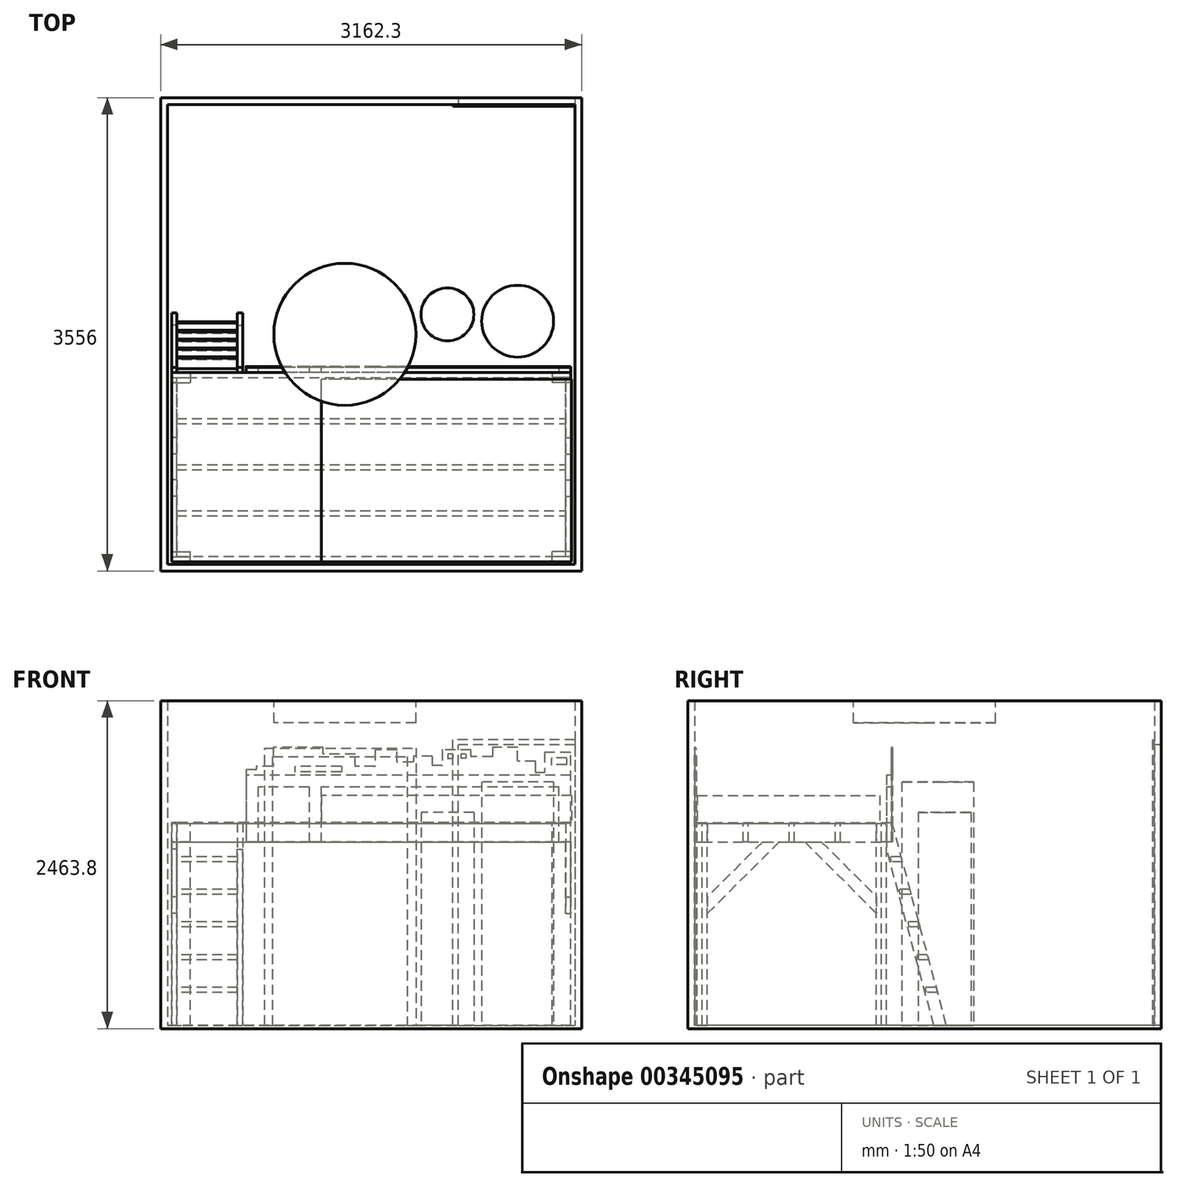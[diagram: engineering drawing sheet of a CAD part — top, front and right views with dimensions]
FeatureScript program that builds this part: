
annotation { "Feature Type Name" : "Feature", "Feature Type Description" : "" }
export const myFeature = defineFeature(function(context is Context, id is Id, definition is map)
    precondition{}
    {
        {
            var Q0;
            Q0=qCreatedBy(makeId("Top.planeOp"),FACE);
            var sketch = newSketch(context, id + "F0", { "sketchPlane" : qUnion([Q0])});
            skLineSegment(sketch, "E0.bottom", {"start": v(-2262.88, 2923.08) * mm, "end": v(-56.88, 2923.08) * mm});
            skLineSegment(sketch, "E0.top", {"start": v(-2262.88, -531.32) * mm, "end": v(797.82, -531.32) * mm});
            skLineSegment(sketch, "E0.left", {"start": v(-2262.88, 2923.08) * mm, "end": v(-2262.88, -531.32) * mm});
            skLineSegment(sketch, "E0.right", {"start": v(797.82, 2923.08) * mm, "end": v(797.82, -531.32) * mm});
            skLineSegment(sketch, "E1.0", {"start": v(-2313.68, 2973.88) * mm, "end": v(-56.88, 2973.88) * mm});
            skLineSegment(sketch, "E1.1", {"start": v(-2313.68, 2973.88) * mm, "end": v(-2313.68, -582.12) * mm});
            skLineSegment(sketch, "E1.2", {"start": v(-2313.68, -582.12) * mm, "end": v(848.62, -582.12) * mm});
            skLineSegment(sketch, "E1.3", {"start": v(848.62, 2973.88) * mm, "end": v(848.62, -582.12) * mm});
            skLineSegment(sketch, "E2.bottom", {"start": v(-94.98, 2923.08) * mm, "end": v(-56.88, 2923.08) * mm});
            skLineSegment(sketch, "E2.top", {"start": v(-94.98, 2910.38) * mm, "end": v(-56.88, 2910.38) * mm});
            skLineSegment(sketch, "E2.left", {"start": v(-94.98, 2923.08) * mm, "end": v(-94.98, 2910.38) * mm});
            skLineSegment(sketch, "E2.right", {"start": v(-56.88, 2923.08) * mm, "end": v(-56.88, 2910.38) * mm});
            skLineSegment(sketch, "E3", {"start": v(-56.88, 2923.08) * mm, "end": v(-56.88, 2973.88) * mm});
            skLineSegment(sketch, "E4", {"start": v(848.62, 2973.88) * mm, "end": v(797.82, 2973.88) * mm});
            skLineSegment(sketch, "E5", {"start": v(797.82, 2973.88) * mm, "end": v(797.82, 2923.08) * mm});
            skLineSegment(sketch, "E6", {"start": v(-56.88, 2973.88) * mm, "end": v(797.82, 2973.88) * mm});
            skLineSegment(sketch, "E7", {"start": v(797.82, 2923.08) * mm, "end": v(-56.88, 2923.08) * mm});
            skSolve(sketch);
        }
        {
            var Q0;
            Q0 = qSketchRegion(id + "F0", true);
            extrude(context, id + "F1", {"entities" : qUnion([Q0]), "depth" : 2438.4 * mm});
        }
        {
            var Q0;
            Q0=makeQuery(id+"F1.opExtrude","SWEPT_FACE",FACE,{"disambiguationData":[OSD([sQuery(id+"F0.wireOp",EDGE,"E0.bottom"),sQuery(id+"F0.wireOp",EDGE,"E2.bottom"),sQuery(id+"F0.wireOp",EDGE,"E7")])]});
            var sketch = newSketch(context, id + "F2", { "sketchPlane" : qUnion([Q0])});
            skLineSegment(sketch, "E8.bottom", {"start": v(797.82, 0) * mm, "end": v(-78.48, 0) * mm});
            skLineSegment(sketch, "E8.top", {"start": v(797.82, 2108.2) * mm, "end": v(-78.48, 2108.2) * mm});
            skLineSegment(sketch, "E8.left", {"start": v(797.82, 0) * mm, "end": v(797.82, 2108.2) * mm});
            skLineSegment(sketch, "E8.right", {"start": v(-78.48, 0) * mm, "end": v(-78.48, 2108.2) * mm});
            skSolve(sketch);
        }
        {
            var Q0;
            Q0 = qSketchRegion(id + "F2", true);
            extrude(context, id + "F3", {"entities" : qUnion([Q0]), "operationType" : NewBodyOperationType.REMOVE, "endBound" : BoundingType.UP_TO_NEXT, "oppositeDirection" : true, "depth" : 25.4 * mm});
        }
        {
            var Q0;
            Q0=makeQuery(id+"F1.opExtrude","SWEPT_FACE",FACE,{"disambiguationData":[OSD([sQuery(id+"F0.wireOp",EDGE,"E0.bottom"),sQuery(id+"F0.wireOp",EDGE,"E2.bottom"),sQuery(id+"F0.wireOp",EDGE,"E7")])]});
            var sketch = newSketch(context, id + "F4", { "sketchPlane" : qUnion([Q0])});
            skLineSegment(sketch, "E9.bottom", {"start": v(-78.48, 0) * mm, "end": v(-116.58, 0) * mm});
            skLineSegment(sketch, "E9.top", {"start": v(-78.48, 2146.3) * mm, "end": v(-116.58, 2146.3) * mm});
            skLineSegment(sketch, "E9.left", {"start": v(-78.48, 0) * mm, "end": v(-78.48, 2146.3) * mm});
            skLineSegment(sketch, "E9.right", {"start": v(-116.58, 0) * mm, "end": v(-116.58, 2146.3) * mm});
            skLineSegment(sketch, "E10.bottom", {"start": v(-78.48, 2146.3) * mm, "end": v(797.82, 2146.3) * mm});
            skLineSegment(sketch, "E10.top", {"start": v(-78.48, 2108.2) * mm, "end": v(797.82, 2108.2) * mm});
            skLineSegment(sketch, "E10.left", {"start": v(-78.48, 2146.3) * mm, "end": v(-78.48, 2108.2) * mm});
            skLineSegment(sketch, "E10.right", {"start": v(797.82, 2146.3) * mm, "end": v(797.82, 2108.2) * mm});
            skSolve(sketch);
        }
        {
            var Q0;
            Q0 = qSketchRegion(id + "F4", true);
            extrude(context, id + "F5", {"entities" : qUnion([Q0]), "operationType" : NewBodyOperationType.ADD, "depth" : 12.7 * mm});
        }
        {
            var Q0;
            Q0=makeQuery(id+"F1.opExtrude","CAP_FACE",FACE,{"disambiguationData":[OSD([sQuery(id+"F0.wireOp",EDGE,"E0.bottom"),sQuery(id+"F0.wireOp",EDGE,"E0.top"),sQuery(id+"F0.wireOp",EDGE,"E0.left"),sQuery(id+"F0.wireOp",EDGE,"E0.right"),sQuery(id+"F0.wireOp",EDGE,"E1.0"),sQuery(id+"F0.wireOp",EDGE,"E1.1"),sQuery(id+"F0.wireOp",EDGE,"E1.2"),sQuery(id+"F0.wireOp",EDGE,"E1.3"),sQuery(id+"F0.wireOp",EDGE,"E2.bottom"),sQuery(id+"F0.wireOp",EDGE,"E4"),sQuery(id+"F0.wireOp",EDGE,"E6"),sQuery(id+"F0.wireOp",EDGE,"E7")])],"isStart":false});
            var sketch = newSketch(context, id + "F6", { "sketchPlane" : qUnion([Q0])});
            skCircle(sketch, "E11", {"center": v(-929.38, 1195.88) * mm, "radius": 533.4 * mm});
            skSolve(sketch);
        }
        {
            var Q0;
            Q0 = qSketchRegion(id + "F6", true);
            extrude(context, id + "F7", {"entities" : qUnion([Q0]), "oppositeDirection" : true, "depth" : 165.1 * mm});
        }
        {
            var Q0;
            Q0=makeQuery(id+"F5.boolean.opBoolean","MERGE",FACE,{"derivedFrom":[makeQuery(id+"F1.opExtrude","CAP_FACE",FACE,{"disambiguationData":[OSD([sQuery(id+"F0.wireOp",EDGE,"E0.bottom"),sQuery(id+"F0.wireOp",EDGE,"E0.top"),sQuery(id+"F0.wireOp",EDGE,"E0.left"),sQuery(id+"F0.wireOp",EDGE,"E0.right"),sQuery(id+"F0.wireOp",EDGE,"E1.0"),sQuery(id+"F0.wireOp",EDGE,"E1.1"),sQuery(id+"F0.wireOp",EDGE,"E1.2"),sQuery(id+"F0.wireOp",EDGE,"E1.3"),sQuery(id+"F0.wireOp",EDGE,"E2.bottom"),sQuery(id+"F0.wireOp",EDGE,"E4"),sQuery(id+"F0.wireOp",EDGE,"E6"),sQuery(id+"F0.wireOp",EDGE,"E7")])],"isStart":true}),makeQuery(id+"F5.opExtrude","SWEPT_FACE",FACE,{"disambiguationData":[OSD([sQuery(id+"F4.wireOp",EDGE,"E9.bottom")])]})]});
            var sketch = newSketch(context, id + "F8", { "sketchPlane" : qUnion([Q0])});
            skLineSegment(sketch, "E12.bottom", {"start": v(-2313.68, -2973.88) * mm, "end": v(848.62, -2973.88) * mm});
            skLineSegment(sketch, "E12.top", {"start": v(-2313.68, 582.12) * mm, "end": v(848.62, 582.12) * mm});
            skLineSegment(sketch, "E12.left", {"start": v(-2313.68, -2973.88) * mm, "end": v(-2313.68, 582.12) * mm});
            skLineSegment(sketch, "E12.right", {"start": v(848.62, -2973.88) * mm, "end": v(848.62, 582.12) * mm});
            skSolve(sketch);
        }
        {
            var Q0;
            Q0 = qSketchRegion(id + "F8", true);
            extrude(context, id + "F9", {"entities" : qUnion([Q0]), "operationType" : NewBodyOperationType.ADD, "depth" : 25.4 * mm});
        }
        {
            var Q0;
            Q0=makeQuery(id+"F9.opExtrude","CAP_FACE",FACE,{"disambiguationData":[OSD([sQuery(id+"F8.wireOp",EDGE,"E12.bottom"),sQuery(id+"F8.wireOp",EDGE,"E12.top"),sQuery(id+"F8.wireOp",EDGE,"E12.left"),sQuery(id+"F8.wireOp",EDGE,"E12.right")])],"isStart":true});
            cPlane(context, id + "F10", {"entities" : qUnion([Q0]), "cplaneType" : CPlaneType.OFFSET, "offset" : 1524 * mm, "width" : 152.4 * mm, "height" : 152.4 * mm});
        }
        {
            var Q0;
            Q0=makeQuery(id+"F1.opExtrude","SWEPT_FACE",FACE,{"disambiguationData":[OSD([sQuery(id+"F0.wireOp",EDGE,"E0.top")])]});
            var sketch = newSketch(context, id + "F11", { "sketchPlane" : qUnion([Q0])});
            skLineSegment(sketch, "E13.bottom", {"start": v(1532.63, 0) * mm, "end": v(1469.13, 0) * mm});
            skLineSegment(sketch, "E13.top", {"start": v(1532.63, 2082.8) * mm, "end": v(1469.13, 2082.8) * mm});
            skLineSegment(sketch, "E13.left", {"start": v(1532.63, 0) * mm, "end": v(1532.63, 2082.8) * mm});
            skLineSegment(sketch, "E13.right", {"start": v(1469.13, 0) * mm, "end": v(1469.13, 2082.8) * mm});
            skLineSegment(sketch, "E14.bottom", {"start": v(1469.13, 2082.8) * mm, "end": v(459.48, 2082.8) * mm});
            skLineSegment(sketch, "E14.top", {"start": v(1469.13, 2019.3) * mm, "end": v(459.48, 2019.3) * mm});
            skLineSegment(sketch, "E14.left", {"start": v(1469.13, 2082.8) * mm, "end": v(1469.13, 2019.3) * mm});
            skLineSegment(sketch, "E14.right", {"start": v(459.48, 2082.8) * mm, "end": v(459.48, 2019.3) * mm});
            skLineSegment(sketch, "E15.bottom", {"start": v(459.48, 2082.8) * mm, "end": v(395.98, 2082.8) * mm});
            skLineSegment(sketch, "E15.top", {"start": v(459.48, 0) * mm, "end": v(395.98, 0) * mm});
            skLineSegment(sketch, "E15.left", {"start": v(459.48, 2082.8) * mm, "end": v(459.48, 0) * mm});
            skLineSegment(sketch, "E15.right", {"start": v(395.98, 2082.8) * mm, "end": v(395.98, 0) * mm});
            skSolve(sketch);
        }
        {
            var Q0;
            Q0 = qSketchRegion(id + "F11", true);
            extrude(context, id + "F12", {"entities" : qUnion([Q0]), "operationType" : NewBodyOperationType.ADD, "depth" : 12.7 * mm});
        }
        {
            var Q0;
            Q0=qCreatedBy(id+"F10.planeOp",FACE);
            var sketch = newSketch(context, id + "F13", { "sketchPlane" : qUnion([Q0])});
            skLineSegment(sketch, "E16.bottom", {"start": v(772.42, -512.27) * mm, "end": v(-1107.18, -512.27) * mm});
            skLineSegment(sketch, "E16.top", {"start": v(772.42, 859.33) * mm, "end": v(-1107.18, 859.33) * mm});
            skLineSegment(sketch, "E16.left", {"start": v(772.42, -512.27) * mm, "end": v(772.42, 859.33) * mm});
            skLineSegment(sketch, "E16.right", {"start": v(-1107.18, -512.27) * mm, "end": v(-1107.18, 859.33) * mm});
            skSolve(sketch);
        }
        {
            var Q0;
            Q0 = qSketchRegion(id + "F13", true);
            extrude(context, id + "F14", {"entities" : qUnion([Q0]), "depth" : 203.2 * mm});
        }
        {
            var Q0;
            Q0=qCreatedBy(id+"F10.planeOp",FACE);
            var sketch = newSketch(context, id + "F15", { "sketchPlane" : qUnion([Q0])});
            skLineSegment(sketch, "E17.bottom", {"start": v(766.07, -512.27) * mm, "end": v(-2231.13, -512.27) * mm});
            skLineSegment(sketch, "E17.top", {"start": v(766.07, 910.13) * mm, "end": v(-2231.13, 910.13) * mm});
            skLineSegment(sketch, "E17.left", {"start": v(766.07, -512.27) * mm, "end": v(766.07, 910.13) * mm});
            skLineSegment(sketch, "E17.right", {"start": v(-2231.13, -512.27) * mm, "end": v(-2231.13, 910.13) * mm});
            skSolve(sketch);
        }
        {
            var Q0;
            Q0 = qSketchRegion(id + "F15", true);
            extrude(context, id + "F16", {"entities" : qUnion([Q0]), "oppositeDirection" : true, "depth" : 6.35 * mm});
        }
        {
            var Q0;
            Q0=makeQuery(id+"F16.opExtrude","CAP_FACE",FACE,{"disambiguationData":[OSD([sQuery(id+"F15.wireOp",EDGE,"E17.bottom"),sQuery(id+"F15.wireOp",EDGE,"E17.top"),sQuery(id+"F15.wireOp",EDGE,"E17.left"),sQuery(id+"F15.wireOp",EDGE,"E17.right")])],"isStart":false});
            var sketch = newSketch(context, id + "F17", { "sketchPlane" : qUnion([Q0])});
            skLineSegment(sketch, "E18.bottom", {"start": v(-2231.13, 474.17) * mm, "end": v(-2193.03, 474.17) * mm});
            skLineSegment(sketch, "E18.top", {"start": v(-2231.13, -872.03) * mm, "end": v(-2193.03, -872.03) * mm});
            skLineSegment(sketch, "E18.left", {"start": v(-2231.13, 474.17) * mm, "end": v(-2231.13, -872.03) * mm});
            skLineSegment(sketch, "E18.right", {"start": v(-2193.03, 474.17) * mm, "end": v(-2193.03, -872.03) * mm});
            skLineSegment(sketch, "E19.bottom", {"start": v(766.07, 474.17) * mm, "end": v(727.97, 474.17) * mm});
            skLineSegment(sketch, "E19.top", {"start": v(766.07, -872.03) * mm, "end": v(727.97, -872.03) * mm});
            skLineSegment(sketch, "E19.left", {"start": v(766.07, 474.17) * mm, "end": v(766.07, -872.03) * mm});
            skLineSegment(sketch, "E19.right", {"start": v(727.97, 474.17) * mm, "end": v(727.97, -872.03) * mm});
            skLineSegment(sketch, "E20.0", {"start": v(-2231.13, 512.27) * mm, "end": v(-2231.13, -910.13) * mm, "construction": true});
            skLineSegment(sketch, "E21.0", {"start": v(766.07, 512.27) * mm, "end": v(766.07, -910.13) * mm, "construction": true});
            skSolve(sketch);
        }
        {
            var Q0;
            Q0 = qSketchRegion(id + "F17", true);
            extrude(context, id + "F18", {"entities" : qUnion([Q0]), "depth" : 139.7 * mm});
        }
        {
            var Q0;
            Q0=makeQuery(id+"F16.opExtrude","CAP_FACE",FACE,{"disambiguationData":[OSD([sQuery(id+"F15.wireOp",EDGE,"E17.bottom"),sQuery(id+"F15.wireOp",EDGE,"E17.top"),sQuery(id+"F15.wireOp",EDGE,"E17.left"),sQuery(id+"F15.wireOp",EDGE,"E17.right")])],"isStart":false});
            var sketch = newSketch(context, id + "F19", { "sketchPlane" : qUnion([Q0])});
            skPoint(sketch, "E22.0", {"position": v(-2193.03, 474.17) * mm});
            skPoint(sketch, "E23.0", {"position": v(727.97, 474.17) * mm});
            skPoint(sketch, "E24.0", {"position": v(766.07, -910.13) * mm});
            skPoint(sketch, "E25.0", {"position": v(-2231.13, -910.13) * mm});
            skLineSegment(sketch, "E26.0", {"start": v(766.07, 512.27) * mm, "end": v(-2231.13, 512.27) * mm, "construction": true});
            skLineSegment(sketch, "E27.top", {"start": v(-2231.13, -872.03) * mm, "end": v(766.07, -872.03) * mm});
            skLineSegment(sketch, "E27.right", {"start": v(766.07, -910.13) * mm, "end": v(766.07, -872.03) * mm});
            skLineSegment(sketch, "E28", {"start": v(766.07, -910.13) * mm, "end": v(-2231.13, -910.13) * mm});
            skLineSegment(sketch, "E29", {"start": v(-2231.13, -910.13) * mm, "end": v(-2231.13, -872.03) * mm});
            skLineSegment(sketch, "E30", {"start": v(766.07, -872.03) * mm, "end": v(766.07, -910.13) * mm});
            skLineSegment(sketch, "E31.0.1.0", {"start": v(-2231.13, 512.27) * mm, "end": v(766.07, 512.27) * mm});
            skLineSegment(sketch, "E31.0.1.1", {"start": v(766.07, 474.17) * mm, "end": v(-2231.13, 474.17) * mm});
            skLineSegment(sketch, "E31.0.1.2", {"start": v(766.07, 512.27) * mm, "end": v(766.07, 474.17) * mm});
            skLineSegment(sketch, "E31.0.1.3", {"start": v(-2231.13, 474.17) * mm, "end": v(-2231.13, 512.27) * mm});
            skLineSegment(sketch, "E31.direction1", {"start": v(-2231.13, -872.03) * mm, "end": v(-2165.04, -872.03) * mm, "construction": true});
            skLineSegment(sketch, "E31.direction2", {"start": v(-2231.13, -872.03) * mm, "end": v(-2231.13, 512.27) * mm, "construction": true});
            skPoint(sketch, "E32.0", {"position": v(-2231.13, -872.03) * mm});
            skPoint(sketch, "E33.0", {"position": v(766.07, -872.03) * mm});
            skPoint(sketch, "E34.startSnap0", {"position": v(-732.53, 512.27) * mm});
            skLineSegment(sketch, "E35.0", {"start": v(-2193.03, 474.17) * mm, "end": v(-2193.03, -872.03) * mm, "construction": true});
            skLineSegment(sketch, "E36.0", {"start": v(727.97, 474.17) * mm, "end": v(727.97, -872.03) * mm, "construction": true});
            skLineSegment(sketch, "E37.bottom", {"start": v(-2193.03, -179.88) * mm, "end": v(727.97, -179.88) * mm});
            skLineSegment(sketch, "E37.top", {"start": v(-2193.03, -217.98) * mm, "end": v(727.97, -217.98) * mm});
            skLineSegment(sketch, "E37.left", {"start": v(-2193.03, -179.88) * mm, "end": v(-2193.03, -217.98) * mm});
            skLineSegment(sketch, "E37.right", {"start": v(727.97, -179.88) * mm, "end": v(727.97, -217.98) * mm});
            skPoint(sketch, "E38", {"position": v(-2193.03, -198.93) * mm});
            skPoint(sketch, "E39", {"position": v(727.97, -198.93) * mm});
            skLineSegment(sketch, "E40", {"start": v(-732.53, -179.88) * mm, "end": v(-732.53, 474.17) * mm, "construction": true});
            skLineSegment(sketch, "E41", {"start": v(-732.53, -872.03) * mm, "end": v(-732.53, -217.98) * mm, "construction": true});
            skPoint(sketch, "E42", {"position": v(-732.53, 147.15) * mm});
            skLineSegment(sketch, "E43.left", {"start": v(727.97, 0) * mm, "end": v(727.97, 294.3) * mm});
            skLineSegment(sketch, "E43.right", {"start": v(-2193.03, 0) * mm, "end": v(-2193.03, 294.3) * mm});
            skLineSegment(sketch, "E44.bottom", {"start": v(-2193.03, 128.1) * mm, "end": v(727.97, 128.1) * mm});
            skLineSegment(sketch, "E44.top", {"start": v(-2193.03, 166.2) * mm, "end": v(727.97, 166.2) * mm});
            skLineSegment(sketch, "E44.left", {"start": v(-2193.03, 128.1) * mm, "end": v(-2193.03, 166.2) * mm});
            skLineSegment(sketch, "E44.right", {"start": v(727.97, 128.1) * mm, "end": v(727.97, 166.2) * mm});
            skLineSegment(sketch, "E45", {"start": v(-2193.03, -198.93) * mm, "end": v(727.97, -198.93) * mm, "construction": true});
            skLineSegment(sketch, "E46.MirrorCS", {"start": v(-2193.03, -525.95) * mm, "end": v(727.97, -525.95) * mm});
            skLineSegment(sketch, "E47.MirrorCS", {"start": v(-2193.03, -564.05) * mm, "end": v(727.97, -564.05) * mm});
            skLineSegment(sketch, "E48", {"start": v(-2193.03, -525.95) * mm, "end": v(-2193.03, -564.05) * mm, "construction": true});
            skLineSegment(sketch, "E49", {"start": v(-2193.03, -525.95) * mm, "end": v(-2193.03, -564.05) * mm});
            skLineSegment(sketch, "E50", {"start": v(727.97, -525.95) * mm, "end": v(727.97, -564.05) * mm});
            skSolve(sketch);
        }
        {
            var Q0;
            Q0 = qSketchRegion(id + "F19", true);
            extrude(context, id + "F20", {"entities" : qUnion([Q0]), "depth" : 139.7 * mm});
        }
        {
            var Q0;
            Q0=makeQuery(id+"F18.opExtrude","SWEPT_FACE",FACE,{"disambiguationData":[OSD([sQuery(id+"F17.wireOp",EDGE,"E18.left")])]});
            var sketch = newSketch(context, id + "F21", { "sketchPlane" : qUnion([Q0])});
            skPoint(sketch, "E51.0", {"position": v(-910.13, 1524) * mm});
            skPoint(sketch, "E52.0", {"position": v(-910.13, 1377.95) * mm});
            skLineSegment(sketch, "E53", {"start": v(-910.13, 1524) * mm, "end": v(-948.23, 1524) * mm});
            skLineSegment(sketch, "E54", {"start": v(-948.23, 1524) * mm, "end": v(-1356.58, 0) * mm});
            skLineSegment(sketch, "E55", {"start": v(-1356.58, 0) * mm, "end": v(-1264.54, 0) * mm});
            skLineSegment(sketch, "E56", {"start": v(-1264.54, 0) * mm, "end": v(-910.13, 1322.7) * mm});
            skLineSegment(sketch, "E57", {"start": v(-910.13, 1524) * mm, "end": v(-910.13, 1322.7) * mm});
            skLineSegment(sketch, "E58.0", {"start": v(-2973.88, -25.4) * mm, "end": v(582.12, -25.4) * mm, "construction": true});
            skLineSegment(sketch, "E59.0.0", {"start": v(531.32, 0) * mm, "end": v(518.62, 0) * mm, "construction": true});
            skLineSegment(sketch, "E59.0.2", {"start": v(518.62, 0) * mm, "end": v(531.32, 0) * mm, "construction": true});
            skLineSegment(sketch, "E59.0.4", {"start": v(531.32, 0) * mm, "end": v(-2973.88, 0) * mm, "construction": true});
            skLineSegment(sketch, "E59.0.6", {"start": v(-2973.88, 0) * mm, "end": v(-2910.38, 0) * mm, "construction": true});
            skLineSegment(sketch, "E59.0.8", {"start": v(-2910.38, 0) * mm, "end": v(-2923.08, 0) * mm, "construction": true});
            skLineSegment(sketch, "E59.0.10", {"start": v(-2923.08, 0) * mm, "end": v(531.32, 0) * mm, "construction": true});
            skLineSegment(sketch, "E59.0.12", {"start": v(531.32, 0) * mm, "end": v(518.62, 0) * mm, "construction": true});
            skLineSegment(sketch, "E59.0.14", {"start": v(518.62, 0) * mm, "end": v(531.32, 0) * mm, "construction": true});
            skSolve(sketch);
        }
        {
            var Q0;
            Q0 = qSketchRegion(id + "F21", true);
            extrude(context, id + "F22", {"entities" : qUnion([Q0]), "oppositeDirection" : true, "depth" : 38.1 * mm});
        }
        {
            var Q0;
            Q0=makeQuery(id+"F22.opExtrude","CAP_FACE",FACE,{"disambiguationData":[OSD([sQuery(id+"F21.wireOp",EDGE,"E53"),sQuery(id+"F21.wireOp",EDGE,"E54"),sQuery(id+"F21.wireOp",EDGE,"E55"),sQuery(id+"F21.wireOp",EDGE,"E56"),sQuery(id+"F21.wireOp",EDGE,"E57")])],"isStart":false});
            var sketch = newSketch(context, id + "F23", { "sketchPlane" : qUnion([Q0])});
            skLineSegment(sketch, "E60.bottom", {"start": v(1280.33, 284.57) * mm, "end": v(1201.64, 284.57) * mm});
            skLineSegment(sketch, "E60.top", {"start": v(1290.54, 246.47) * mm, "end": v(1204.18, 246.47) * mm});
            skLineSegment(sketch, "E60.left", {"start": v(1280.33, 284.57) * mm, "end": v(1290.54, 246.47) * mm});
            skLineSegment(sketch, "E60.right", {"start": v(1201.64, 284.57) * mm, "end": v(1204.18, 246.47) * mm});
            skLineSegment(sketch, "E61.0.1.0", {"start": v(1214.59, 529.92) * mm, "end": v(1135.9, 529.92) * mm});
            skLineSegment(sketch, "E61.0.1.1", {"start": v(1224.8, 491.82) * mm, "end": v(1138.44, 491.82) * mm});
            skLineSegment(sketch, "E61.0.1.2", {"start": v(1214.59, 529.92) * mm, "end": v(1224.8, 491.82) * mm});
            skLineSegment(sketch, "E61.0.1.3", {"start": v(1135.9, 529.92) * mm, "end": v(1138.44, 491.82) * mm});
            skLineSegment(sketch, "E61.0.2.0", {"start": v(1148.85, 775.26) * mm, "end": v(1070.16, 775.26) * mm});
            skLineSegment(sketch, "E61.0.2.1", {"start": v(1159.06, 737.16) * mm, "end": v(1072.7, 737.16) * mm});
            skLineSegment(sketch, "E61.0.2.2", {"start": v(1148.85, 775.26) * mm, "end": v(1159.06, 737.16) * mm});
            skLineSegment(sketch, "E61.0.2.3", {"start": v(1070.16, 775.26) * mm, "end": v(1072.7, 737.16) * mm});
            skLineSegment(sketch, "E61.0.3.0", {"start": v(1083.1, 1020.6) * mm, "end": v(1004.42, 1020.6) * mm});
            skLineSegment(sketch, "E61.0.3.1", {"start": v(1093.32, 982.5) * mm, "end": v(1006.96, 982.5) * mm});
            skLineSegment(sketch, "E61.0.3.2", {"start": v(1083.1, 1020.6) * mm, "end": v(1093.32, 982.5) * mm});
            skLineSegment(sketch, "E61.0.3.3", {"start": v(1004.42, 1020.6) * mm, "end": v(1006.96, 982.5) * mm});
            skLineSegment(sketch, "E61.0.4.0", {"start": v(1017.37, 1265.95) * mm, "end": v(938.68, 1265.95) * mm});
            skLineSegment(sketch, "E61.0.4.1", {"start": v(1027.58, 1227.85) * mm, "end": v(941.22, 1227.85) * mm});
            skLineSegment(sketch, "E61.0.4.2", {"start": v(1017.37, 1265.95) * mm, "end": v(1027.58, 1227.85) * mm});
            skLineSegment(sketch, "E61.0.4.3", {"start": v(938.68, 1265.95) * mm, "end": v(941.22, 1227.85) * mm});
            skLineSegment(sketch, "E61.direction1", {"start": v(1204.18, 246.47) * mm, "end": v(1219.52, 246.47) * mm, "construction": true});
            skLineSegment(sketch, "E61.direction2", {"start": v(1204.18, 246.47) * mm, "end": v(1138.44, 491.82) * mm, "construction": true});
            skLineSegment(sketch, "E62.0", {"start": v(948.23, 1524) * mm, "end": v(1356.58, 0) * mm, "construction": true});
            skLineSegment(sketch, "E63", {"start": v(1201.64, 284.57) * mm, "end": v(1211.85, 246.47) * mm});
            skSolve(sketch);
        }
        {
            var Q0;
            Q0 = qSketchRegion(id + "F23", true);
            extrude(context, id + "F24", {"entities" : qUnion([Q0]), "depth" : 457.2 * mm});
        }
        {
            var Q0;
            Q0=makeQuery(id+"F22.opExtrude","CAP_FACE",FACE,{"disambiguationData":[OSD([sQuery(id+"F21.wireOp",EDGE,"E53"),sQuery(id+"F21.wireOp",EDGE,"E54"),sQuery(id+"F21.wireOp",EDGE,"E55"),sQuery(id+"F21.wireOp",EDGE,"E56"),sQuery(id+"F21.wireOp",EDGE,"E57")])],"isStart":true});
            cPlane(context, id + "F25", {"entities" : qUnion([Q0]), "cplaneType" : CPlaneType.OFFSET, "offset" : 266.7 * mm, "oppositeDirection" : true, "width" : 152.4 * mm, "height" : 152.4 * mm});
        }
        {
            var Q0;
            Q0=makeQuery(id+"F22.opExtrude","SWEPT_BODY",BODY,{"disambiguationData":[OSD([sQuery(id+"F21.wireOp",EDGE,"E53"),sQuery(id+"F21.wireOp",EDGE,"E54"),sQuery(id+"F21.wireOp",EDGE,"E55"),sQuery(id+"F21.wireOp",EDGE,"E56"),sQuery(id+"F21.wireOp",EDGE,"E57")])]});
            var Q1;
            Q1=qCreatedBy(id+"F25.planeOp",FACE);
            mirror(context, id + "F26", {"entities" : qUnion([Q0]), "mirrorPlane" : qUnion([Q1])});
        }
        {
            var Q0;
            Q0=makeQuery(id+"F20.opExtrude","SWEPT_FACE",FACE,{"disambiguationData":[OSD([sQuery(id+"F19.wireOp",EDGE,"E28")])]});
            var sketch = newSketch(context, id + "F27", { "sketchPlane" : qUnion([Q0])});
            skLineSegment(sketch, "E64.0", {"start": v(-766.07, 1377.95) * mm, "end": v(-766.07, 1517.65) * mm, "construction": true});
            skLineSegment(sketch, "E65.0", {"start": v(-766.07, 1377.95) * mm, "end": v(2231.13, 1377.95) * mm, "construction": true});
            skPoint(sketch, "E66.0", {"position": v(-747.02, 1377.95) * mm});
            skLineSegment(sketch, "E67.bottom", {"start": v(-766.07, 1377.95) * mm, "end": v(-677.17, 1377.95) * mm});
            skLineSegment(sketch, "E67.top", {"start": v(-766.07, 1879.6) * mm, "end": v(-677.17, 1879.6) * mm});
            skLineSegment(sketch, "E67.left", {"start": v(-766.07, 1377.95) * mm, "end": v(-766.07, 1879.6) * mm});
            skLineSegment(sketch, "E67.right", {"start": v(-677.17, 1377.95) * mm, "end": v(-677.17, 1879.6) * mm});
            skLineSegment(sketch, "E68.bottom", {"start": v(-677.17, 1879.6) * mm, "end": v(1672.33, 1879.6) * mm});
            skLineSegment(sketch, "E68.top", {"start": v(-677.17, 1790.7) * mm, "end": v(1672.33, 1790.7) * mm});
            skLineSegment(sketch, "E68.left", {"start": v(-677.17, 1879.6) * mm, "end": v(-677.17, 1790.7) * mm});
            skLineSegment(sketch, "E68.right", {"start": v(1672.33, 1879.6) * mm, "end": v(1672.33, 1790.7) * mm});
            skLineSegment(sketch, "E69.bottom", {"start": v(1672.33, 1790.7) * mm, "end": v(1583.43, 1790.7) * mm});
            skLineSegment(sketch, "E69.top", {"start": v(1672.33, 1377.95) * mm, "end": v(1583.43, 1377.95) * mm});
            skLineSegment(sketch, "E69.left", {"start": v(1672.33, 1790.7) * mm, "end": v(1672.33, 1377.95) * mm});
            skLineSegment(sketch, "E69.right", {"start": v(1583.43, 1790.7) * mm, "end": v(1583.43, 1377.95) * mm});
            skLineSegment(sketch, "E70.bottom", {"start": v(1109.23, 1790.7) * mm, "end": v(1198.13, 1790.7) * mm});
            skLineSegment(sketch, "E70.top", {"start": v(1109.23, 1377.95) * mm, "end": v(1198.13, 1377.95) * mm});
            skLineSegment(sketch, "E70.left", {"start": v(1109.23, 1790.7) * mm, "end": v(1109.23, 1377.95) * mm});
            skLineSegment(sketch, "E70.right", {"start": v(1198.13, 1790.7) * mm, "end": v(1198.13, 1377.95) * mm});
            skLineSegment(sketch, "E71.0", {"start": v(1697.73, 1524) * mm, "end": v(1697.73, 1322.7) * mm, "construction": true});
            skSolve(sketch);
        }
        {
            var Q0;
            Q0 = qSketchRegion(id + "F27", true);
            extrude(context, id + "F28", {"entities" : qUnion([Q0]), "depth" : 38.1 * mm});
        }
        {
            var Q0;
            Q0=makeQuery(id+"F28.opExtrude","CAP_FACE",FACE,{"disambiguationData":[OSD([sQuery(id+"F27.wireOp",EDGE,"E67.bottom"),sQuery(id+"F27.wireOp",EDGE,"E67.top"),sQuery(id+"F27.wireOp",EDGE,"E67.left"),sQuery(id+"F27.wireOp",EDGE,"E67.right"),sQuery(id+"F27.wireOp",EDGE,"E68.bottom"),sQuery(id+"F27.wireOp",EDGE,"E68.top"),sQuery(id+"F27.wireOp",EDGE,"E68.right"),sQuery(id+"F27.wireOp",EDGE,"E69.top"),sQuery(id+"F27.wireOp",EDGE,"E69.left"),sQuery(id+"F27.wireOp",EDGE,"E69.right"),sQuery(id+"F27.wireOp",EDGE,"E70.top"),sQuery(id+"F27.wireOp",EDGE,"E70.left"),sQuery(id+"F27.wireOp",EDGE,"E70.right")])],"isStart":false});
            var sketch = newSketch(context, id + "F29", { "sketchPlane" : qUnion([Q0])});
            skArc(sketch, "E72", {"start": v(22.49, 1879.6) * mm, "mid": v(-371.79, 2067.27) * mm, "end": v(-766.07, 1879.6) * mm});
            skArc(sketch, "E73", {"start": v(22.49, 1879.6) * mm, "mid": v(416.76, 1691.93) * mm, "end": v(811.04, 1879.6) * mm});
            skArc(sketch, "E74", {"start": v(1599.6, 1879.6) * mm, "mid": v(1205.32, 2067.27) * mm, "end": v(811.04, 1879.6) * mm});
            skLineSegment(sketch, "E75", {"start": v(-371.79, 1559.27) * mm, "end": v(1205.32, 1559.27) * mm, "construction": true});
            skLineSegment(sketch, "E76", {"start": v(-1398.03, 2199.93) * mm, "end": v(1531.6, 2199.93) * mm, "construction": true});
            skLineSegment(sketch, "E77", {"start": v(22.49, 1879.6) * mm, "end": v(-766.07, 1879.6) * mm, "construction": true});
            skLineSegment(sketch, "E78", {"start": v(22.49, 1879.6) * mm, "end": v(1599.6, 1879.6) * mm, "construction": true});
            skSolve(sketch);
        }
        {
            var Q0;
            {var subQ0=sQuery(id+"F29.wireOp",EDGE,"E73");var subQ3=sQuery(id+"F27.wireOp",EDGE,"E68.top");var subQ4=makeQuery(id+"F28.opExtrude","CAP_EDGE",EDGE,{"disambiguationData":[OSD([subQ3]),TDD([makeQuery(id+"F27.imprint","IMPRINT",EDGE,{"disambiguationData":[TD([[makeQuery(id+"F27.imprint","INTERSECT",VERTEX,{"derivedFrom":[sQuery(id+"F27.wireOp",EDGE,"E67.right"),subQ3,sQuery(id+"F27.wireOp",EDGE,"E68.left")]}),-1.0]])],"derivedFrom":subQ3})])],"isStart":false});var subQ5=makeQuery(id+"F29.imprint","INTERSECT",VERTEX,{"disambiguationData":[OD(0.0)],"derivedFrom":[subQ4,subQ0]});Q0=makeQuery(id+"F29.imprint","IMPRINT",FACE,{"disambiguationData":[TD([[makeQuery(id+"F29.imprint","IMPRINT",EDGE,{"disambiguationData":[TD([[subQ5,1.0]])],"derivedFrom":subQ0}),1.0]])]});}
            var sketch = newSketch(context, id + "F30", { "sketchPlane" : qUnion([Q0])});
            skLineSegment(sketch, "E79.0", {"start": v(-766.07, 1377.95) * mm, "end": v(2231.13, 1377.95) * mm, "construction": true});
            skLineSegment(sketch, "E80.0", {"start": v(-766.07, 1377.95) * mm, "end": v(-766.07, 1879.6) * mm, "construction": true});
            skLineSegment(sketch, "E81.0", {"start": v(1672.33, 1879.6) * mm, "end": v(1672.33, 1377.95) * mm, "construction": true});
            skLineSegment(sketch, "E82.bottom", {"start": v(-766.07, 1377.95) * mm, "end": v(1672.33, 1377.95) * mm});
            skLineSegment(sketch, "E82.top", {"start": v(-766.07, 1879.6) * mm, "end": v(1672.33, 1879.6) * mm});
            skLineSegment(sketch, "E82.left", {"start": v(-766.07, 1377.95) * mm, "end": v(-766.07, 1879.6) * mm});
            skLineSegment(sketch, "E82.right", {"start": v(1672.33, 1377.95) * mm, "end": v(1672.33, 1879.6) * mm});
            skLineSegment(sketch, "E83.bottom", {"start": v(-766.07, 1879.6) * mm, "end": v(-606.47, 1879.6) * mm});
            skLineSegment(sketch, "E83.top", {"start": v(-766.07, 2036.28) * mm, "end": v(-606.47, 2036.28) * mm});
            skLineSegment(sketch, "E83.left", {"start": v(-766.07, 1879.6) * mm, "end": v(-766.07, 2036.28) * mm});
            skLineSegment(sketch, "E83.right", {"start": v(-606.47, 1879.6) * mm, "end": v(-606.47, 2036.28) * mm});
            skPoint(sketch, "E84.oppositeSnap0", {"position": v(-606.47, 1957.94) * mm});
            skLineSegment(sketch, "E84.bottom", {"start": v(-536.73, 1879.6) * mm, "end": v(-360.7, 1879.6) * mm});
            skLineSegment(sketch, "E84.top", {"start": v(-536.73, 1957.94) * mm, "end": v(-360.7, 1957.94) * mm});
            skLineSegment(sketch, "E84.left", {"start": v(-536.73, 1879.6) * mm, "end": v(-536.73, 1957.94) * mm});
            skLineSegment(sketch, "E84.right", {"start": v(-360.7, 1879.6) * mm, "end": v(-360.7, 1957.94) * mm});
            skLineSegment(sketch, "E85.bottom", {"start": v(-410.53, 1957.94) * mm, "end": v(-201.3, 1957.94) * mm});
            skLineSegment(sketch, "E85.top", {"start": v(-410.53, 2116) * mm, "end": v(-201.3, 2116) * mm});
            skLineSegment(sketch, "E85.left", {"start": v(-410.53, 1957.94) * mm, "end": v(-410.53, 2116) * mm});
            skLineSegment(sketch, "E85.right", {"start": v(-201.3, 1957.94) * mm, "end": v(-201.3, 2116) * mm});
            skLineSegment(sketch, "E86.bottom", {"start": v(-360.7, 1957.94) * mm, "end": v(-8.66, 1957.94) * mm});
            skLineSegment(sketch, "E86.top", {"start": v(-360.7, 1879.6) * mm, "end": v(-8.66, 1879.6) * mm});
            skLineSegment(sketch, "E86.left", {"start": v(-360.7, 1957.94) * mm, "end": v(-360.7, 1879.6) * mm});
            skLineSegment(sketch, "E86.right", {"start": v(-8.66, 1957.94) * mm, "end": v(-8.66, 1879.6) * mm});
            skLineSegment(sketch, "E87.bottom", {"start": v(0, 1957.94) * mm, "end": v(183.96, 1957.94) * mm});
            skLineSegment(sketch, "E87.top", {"start": v(0, 2062.85) * mm, "end": v(183.96, 2062.85) * mm});
            skLineSegment(sketch, "E87.left", {"start": v(0, 1957.94) * mm, "end": v(0, 2062.85) * mm});
            skLineSegment(sketch, "E87.right", {"start": v(183.96, 1957.94) * mm, "end": v(183.96, 2062.85) * mm});
            skLineSegment(sketch, "E88.bottom", {"start": v(223.92, 1879.6) * mm, "end": v(363.3, 1879.6) * mm});
            skLineSegment(sketch, "E88.top", {"start": v(223.92, 2076.14) * mm, "end": v(363.3, 2076.14) * mm});
            skLineSegment(sketch, "E88.left", {"start": v(223.92, 1879.6) * mm, "end": v(223.92, 2076.14) * mm});
            skLineSegment(sketch, "E88.right", {"start": v(363.3, 1879.6) * mm, "end": v(363.3, 2076.14) * mm});
            skLineSegment(sketch, "E89.bottom", {"start": v(363.3, 1977.87) * mm, "end": v(592.47, 1977.87) * mm});
            skLineSegment(sketch, "E89.top", {"start": v(363.3, 1879.6) * mm, "end": v(592.47, 1879.6) * mm});
            skLineSegment(sketch, "E89.left", {"start": v(363.3, 1977.87) * mm, "end": v(363.3, 1879.6) * mm});
            skLineSegment(sketch, "E89.right", {"start": v(592.47, 1977.87) * mm, "end": v(592.47, 1879.6) * mm});
            skLineSegment(sketch, "E90.bottom", {"start": v(512.76, 1977.87) * mm, "end": v(682.14, 1977.87) * mm});
            skLineSegment(sketch, "E90.top", {"start": v(512.76, 2096.06) * mm, "end": v(682.14, 2096.06) * mm});
            skLineSegment(sketch, "E90.left", {"start": v(512.76, 1977.87) * mm, "end": v(512.76, 2096.06) * mm});
            skLineSegment(sketch, "E90.right", {"start": v(682.14, 1977.87) * mm, "end": v(682.14, 2096.06) * mm});
            skLineSegment(sketch, "E91.bottom", {"start": v(592.47, 1977.87) * mm, "end": v(961.12, 1977.87) * mm});
            skLineSegment(sketch, "E91.top", {"start": v(592.47, 1879.6) * mm, "end": v(961.12, 1879.6) * mm});
            skLineSegment(sketch, "E92.top", {"start": v(881.4, 1879.6) * mm, "end": v(1200.24, 1879.6) * mm});
            skLineSegment(sketch, "E93.bottom", {"start": v(831.6, 2072.82) * mm, "end": v(1080.68, 2072.82) * mm});
            skLineSegment(sketch, "E93.top", {"start": v(831.6, 1879.6) * mm, "end": v(1080.68, 1879.6) * mm});
            skLineSegment(sketch, "E93.left", {"start": v(831.6, 2072.82) * mm, "end": v(831.6, 1879.6) * mm});
            skLineSegment(sketch, "E93.right", {"start": v(1080.68, 2072.82) * mm, "end": v(1080.68, 1879.6) * mm});
            skLineSegment(sketch, "E94.bottom", {"start": v(1080.68, 2006.4) * mm, "end": v(1200.24, 2006.4) * mm});
            skLineSegment(sketch, "E95.bottom", {"start": v(1392.87, 1879.6) * mm, "end": v(1160.39, 1879.6) * mm});
            skLineSegment(sketch, "E95.top", {"start": v(1392.87, 2076.14) * mm, "end": v(1160.39, 2076.14) * mm});
            skLineSegment(sketch, "E95.left", {"start": v(1392.87, 1879.6) * mm, "end": v(1392.87, 2076.14) * mm});
            skLineSegment(sketch, "E95.right", {"start": v(1160.39, 1879.6) * mm, "end": v(1160.39, 2076.14) * mm});
            skLineSegment(sketch, "E96.bottom", {"start": v(1618.82, 1879.6) * mm, "end": v(1392.87, 1879.6) * mm});
            skLineSegment(sketch, "E96.top", {"start": v(1618.82, 1977.87) * mm, "end": v(1392.87, 1977.87) * mm});
            skLineSegment(sketch, "E96.left", {"start": v(1618.82, 1879.6) * mm, "end": v(1618.82, 1977.87) * mm});
            skLineSegment(sketch, "E96.right", {"start": v(1392.87, 1879.6) * mm, "end": v(1392.87, 1977.87) * mm});
            skLineSegment(sketch, "E97.bottom", {"start": v(1618.82, 1928.73) * mm, "end": v(1672.33, 1928.73) * mm});
            skLineSegment(sketch, "E97.top", {"start": v(1618.82, 1879.6) * mm, "end": v(1672.33, 1879.6) * mm});
            skLineSegment(sketch, "E97.left", {"start": v(1618.82, 1928.73) * mm, "end": v(1618.82, 1879.6) * mm});
            skLineSegment(sketch, "E97.right", {"start": v(1672.33, 1928.73) * mm, "end": v(1672.33, 1879.6) * mm});
            skLineSegment(sketch, "E98.bottom", {"start": v(-700.07, 2000.78) * mm, "end": v(-606.18, 2000.78) * mm});
            skLineSegment(sketch, "E98.top", {"start": v(-700.07, 1942.41) * mm, "end": v(-606.18, 1942.41) * mm});
            skLineSegment(sketch, "E98.left", {"start": v(-700.07, 2000.78) * mm, "end": v(-700.07, 1942.41) * mm});
            skLineSegment(sketch, "E98.right", {"start": v(-606.18, 2000.78) * mm, "end": v(-606.18, 1942.41) * mm});
            skPoint(sketch, "E99.oppositeSnap0", {"position": v(1276.63, 1879.6) * mm});
            skLineSegment(sketch, "E99.bottom", {"start": v(936.03, 1936.27) * mm, "end": v(1276.63, 1936.27) * mm});
            skLineSegment(sketch, "E99.top", {"start": v(936.03, 1883.08) * mm, "end": v(1276.63, 1883.08) * mm});
            skLineSegment(sketch, "E99.left", {"start": v(936.03, 1936.27) * mm, "end": v(936.03, 1883.08) * mm});
            skLineSegment(sketch, "E99.right", {"start": v(1276.63, 1936.27) * mm, "end": v(1276.63, 1883.08) * mm});
            skSolve(sketch);
        }
        {
            var Q0;
            Q0=makeQuery(id+"F28.opExtrude","CAP_FACE",FACE,{"disambiguationData":[OSD([sQuery(id+"F27.wireOp",EDGE,"E67.bottom"),sQuery(id+"F27.wireOp",EDGE,"E67.top"),sQuery(id+"F27.wireOp",EDGE,"E67.left"),sQuery(id+"F27.wireOp",EDGE,"E67.right"),sQuery(id+"F27.wireOp",EDGE,"E68.bottom"),sQuery(id+"F27.wireOp",EDGE,"E68.top"),sQuery(id+"F27.wireOp",EDGE,"E68.right"),sQuery(id+"F27.wireOp",EDGE,"E69.top"),sQuery(id+"F27.wireOp",EDGE,"E69.left"),sQuery(id+"F27.wireOp",EDGE,"E69.right"),sQuery(id+"F27.wireOp",EDGE,"E70.top"),sQuery(id+"F27.wireOp",EDGE,"E70.left"),sQuery(id+"F27.wireOp",EDGE,"E70.right")])],"isStart":false});
            var sketch = newSketch(context, id + "F31", { "sketchPlane" : qUnion([Q0])});
            skLineSegment(sketch, "E100.0", {"start": v(-766.07, 1377.95) * mm, "end": v(1672.33, 1377.95) * mm, "construction": true});
            skLineSegment(sketch, "E101.0", {"start": v(-772.42, 1727.2) * mm, "end": v(1107.18, 1727.2) * mm, "construction": true});
            skLineSegment(sketch, "E102.0", {"start": v(-766.07, 1879.6) * mm, "end": v(1672.33, 1879.6) * mm, "construction": true});
            skLineSegment(sketch, "E103", {"start": v(-799.2, 2089.15) * mm, "end": v(1687.96, 2089.15) * mm, "construction": true});
            skLineSegment(sketch, "E104", {"start": v(-766.07, 1377.95) * mm, "end": v(-766.07, 2050.72) * mm});
            skLineSegment(sketch, "E105", {"start": v(-766.07, 2050.72) * mm, "end": v(-571.05, 2050.72) * mm});
            skLineSegment(sketch, "E106", {"start": v(-571.05, 2050.72) * mm, "end": v(-571.05, 1897.6) * mm});
            skLineSegment(sketch, "E107", {"start": v(-571.05, 1897.6) * mm, "end": v(-503.68, 1897.6) * mm});
            skLineSegment(sketch, "E108", {"start": v(-503.68, 1897.6) * mm, "end": v(-503.68, 1983.35) * mm});
            skLineSegment(sketch, "E109", {"start": v(-503.68, 1983.35) * mm, "end": v(-368.95, 1983.35) * mm});
            skLineSegment(sketch, "E110", {"start": v(-368.95, 1983.35) * mm, "end": v(-368.95, 2089.15) * mm});
            skLineSegment(sketch, "E111", {"start": v(-368.95, 2089.15) * mm, "end": v(-181.81, 2089.15) * mm});
            skLineSegment(sketch, "E112", {"start": v(-181.81, 2089.15) * mm, "end": v(-181.81, 2016.97) * mm});
            skLineSegment(sketch, "E113", {"start": v(-181.81, 2016.97) * mm, "end": v(-18.5, 2016.97) * mm});
            skLineSegment(sketch, "E114", {"start": v(-18.5, 2016.97) * mm, "end": v(-18.5, 2069.09) * mm});
            skLineSegment(sketch, "E115", {"start": v(-18.5, 2069.09) * mm, "end": v(197.9, 2069.09) * mm});
            skLineSegment(sketch, "E116", {"start": v(197.9, 2069.09) * mm, "end": v(197.9, 1950.69) * mm});
            skLineSegment(sketch, "E117", {"start": v(197.9, 1950.69) * mm, "end": v(271.38, 1950.69) * mm});
            skLineSegment(sketch, "E118", {"start": v(271.38, 1950.69) * mm, "end": v(271.38, 2020.4) * mm});
            skLineSegment(sketch, "E119", {"start": v(271.38, 2020.4) * mm, "end": v(414.28, 2020.4) * mm});
            skLineSegment(sketch, "E120", {"start": v(414.28, 2020.4) * mm, "end": v(414.28, 1977.23) * mm});
            skLineSegment(sketch, "E121", {"start": v(414.28, 1977.23) * mm, "end": v(536.76, 1977.23) * mm});
            skLineSegment(sketch, "E122", {"start": v(536.76, 1977.23) * mm, "end": v(536.76, 2069.09) * mm});
            skLineSegment(sketch, "E123", {"start": v(536.76, 2069.09) * mm, "end": v(702.12, 2069.09) * mm});
            skLineSegment(sketch, "E124", {"start": v(702.12, 2069.09) * mm, "end": v(702.12, 1943.7) * mm});
            skLineSegment(sketch, "E125", {"start": v(702.12, 1943.7) * mm, "end": v(851.14, 1943.7) * mm});
            skLineSegment(sketch, "E126", {"start": v(851.14, 1943.7) * mm, "end": v(851.14, 2038.47) * mm});
            skLineSegment(sketch, "E127", {"start": v(851.14, 2038.47) * mm, "end": v(1094.07, 2038.47) * mm});
            skLineSegment(sketch, "E128", {"start": v(1094.07, 2038.47) * mm, "end": v(1094.07, 1983.35) * mm});
            skLineSegment(sketch, "E129", {"start": v(1094.07, 1983.35) * mm, "end": v(1094.07, 2089.15) * mm});
            skLineSegment(sketch, "E130", {"start": v(1094.07, 2089.15) * mm, "end": v(1369.66, 2089.15) * mm});
            skLineSegment(sketch, "E131", {"start": v(1369.66, 2089.15) * mm, "end": v(1467.65, 2089.15) * mm});
            skLineSegment(sketch, "E132", {"start": v(1467.65, 2089.15) * mm, "end": v(1467.65, 1944.56) * mm});
            skLineSegment(sketch, "E133", {"start": v(1467.65, 1944.56) * mm, "end": v(1595.58, 1944.56) * mm});
            skLineSegment(sketch, "E134", {"start": v(1595.58, 1944.56) * mm, "end": v(1595.58, 1918.87) * mm});
            skLineSegment(sketch, "E135", {"start": v(1595.58, 1918.87) * mm, "end": v(1672.33, 1918.87) * mm});
            skLineSegment(sketch, "E136", {"start": v(1672.33, 1918.87) * mm, "end": v(1672.33, 1377.95) * mm});
            skLineSegment(sketch, "E137.bottom", {"start": v(-737.08, 2007.85) * mm, "end": v(-622.76, 2007.85) * mm});
            skLineSegment(sketch, "E137.top", {"start": v(-737.08, 1956.81) * mm, "end": v(-622.76, 1956.81) * mm});
            skLineSegment(sketch, "E137.left", {"start": v(-737.08, 2007.85) * mm, "end": v(-737.08, 1956.81) * mm});
            skLineSegment(sketch, "E137.right", {"start": v(-622.76, 2007.85) * mm, "end": v(-622.76, 1956.81) * mm});
            skLineSegment(sketch, "E138.bottom", {"start": v(953.21, 1944.56) * mm, "end": v(1304.34, 1944.56) * mm});
            skLineSegment(sketch, "E138.top", {"start": v(953.21, 1903.73) * mm, "end": v(1304.34, 1903.73) * mm});
            skLineSegment(sketch, "E138.left", {"start": v(953.21, 1944.56) * mm, "end": v(953.21, 1903.73) * mm});
            skLineSegment(sketch, "E138.right", {"start": v(1304.34, 1944.56) * mm, "end": v(1304.34, 1903.73) * mm});
            skLineSegment(sketch, "E139.bottom", {"start": v(20.29, 2036.43) * mm, "end": v(57.03, 2036.43) * mm});
            skLineSegment(sketch, "E139.top", {"start": v(20.29, 2005.8) * mm, "end": v(57.03, 2005.8) * mm});
            skLineSegment(sketch, "E139.left", {"start": v(20.29, 2036.43) * mm, "end": v(20.29, 2005.8) * mm});
            skLineSegment(sketch, "E139.right", {"start": v(57.03, 2036.43) * mm, "end": v(57.03, 2005.8) * mm});
            skLineSegment(sketch, "E140.bottom", {"start": v(118.27, 2038.47) * mm, "end": v(155.02, 2038.47) * mm});
            skLineSegment(sketch, "E140.top", {"start": v(118.27, 2001.72) * mm, "end": v(155.02, 2001.72) * mm});
            skLineSegment(sketch, "E140.left", {"start": v(118.27, 2038.47) * mm, "end": v(118.27, 2001.72) * mm});
            skLineSegment(sketch, "E140.right", {"start": v(155.02, 2038.47) * mm, "end": v(155.02, 2001.72) * mm});
            skLineSegment(sketch, "E141", {"start": v(-766.07, 1377.95) * mm, "end": v(1672.33, 1377.95) * mm});
            skSolve(sketch);
        }
        {
            var Q0;
            Q0 = qSketchRegion(id + "F31", true);
            extrude(context, id + "F32", {"entities" : qUnion([Q0]), "depth" : 6.35 * mm});
        }
        {
            var Q0;
            Q0=makeQuery(id+"F20.opExtrude","CAP_FACE",FACE,{"disambiguationData":[OSD([sQuery(id+"F19.wireOp",EDGE,"E31.0.1.0"),sQuery(id+"F19.wireOp",EDGE,"E31.0.1.1"),sQuery(id+"F19.wireOp",EDGE,"E31.0.1.2"),sQuery(id+"F19.wireOp",EDGE,"E31.0.1.3")])],"isStart":false});
            var sketch = newSketch(context, id + "F33", { "sketchPlane" : qUnion([Q0])});
            skPoint(sketch, "E142.0", {"position": v(766.07, 512.27) * mm});
            skLineSegment(sketch, "E143.bottom", {"start": v(766.07, 512.27) * mm, "end": v(626.37, 512.27) * mm});
            skLineSegment(sketch, "E143.top", {"start": v(766.07, 474.17) * mm, "end": v(626.37, 474.17) * mm});
            skLineSegment(sketch, "E143.left", {"start": v(766.07, 512.27) * mm, "end": v(766.07, 474.17) * mm});
            skLineSegment(sketch, "E143.right", {"start": v(626.37, 512.27) * mm, "end": v(626.37, 474.17) * mm});
            skPoint(sketch, "E144.0", {"position": v(-2231.13, 512.27) * mm});
            skLineSegment(sketch, "E145.bottom", {"start": v(-2231.13, 512.27) * mm, "end": v(-2091.43, 512.27) * mm});
            skLineSegment(sketch, "E145.top", {"start": v(-2231.13, 474.17) * mm, "end": v(-2091.43, 474.17) * mm});
            skLineSegment(sketch, "E145.left", {"start": v(-2231.13, 512.27) * mm, "end": v(-2231.13, 474.17) * mm});
            skLineSegment(sketch, "E145.right", {"start": v(-2091.43, 512.27) * mm, "end": v(-2091.43, 474.17) * mm});
            skPoint(sketch, "E146.0", {"position": v(-2231.13, -910.13) * mm});
            skLineSegment(sketch, "E147.bottom", {"start": v(-2231.13, -910.13) * mm, "end": v(-2091.43, -910.13) * mm});
            skLineSegment(sketch, "E147.top", {"start": v(-2231.13, -872.03) * mm, "end": v(-2091.43, -872.03) * mm});
            skLineSegment(sketch, "E147.left", {"start": v(-2231.13, -910.13) * mm, "end": v(-2231.13, -872.03) * mm});
            skLineSegment(sketch, "E147.right", {"start": v(-2091.43, -910.13) * mm, "end": v(-2091.43, -872.03) * mm});
            skPoint(sketch, "E148.0", {"position": v(766.07, -910.13) * mm});
            skLineSegment(sketch, "E149.bottom", {"start": v(766.07, -910.13) * mm, "end": v(626.37, -910.13) * mm});
            skLineSegment(sketch, "E149.top", {"start": v(766.07, -872.03) * mm, "end": v(626.37, -872.03) * mm});
            skLineSegment(sketch, "E149.left", {"start": v(766.07, -910.13) * mm, "end": v(766.07, -872.03) * mm});
            skLineSegment(sketch, "E149.right", {"start": v(626.37, -910.13) * mm, "end": v(626.37, -872.03) * mm});
            skSolve(sketch);
        }
        {
            var Q0;
            Q0 = qSketchRegion(id + "F33", true);
            var Q1;
            Q1=makeQuery(id+"F26.opPattern","COPY",FACE,{"derivedFrom":makeQuery(id+"F22.opExtrude","SWEPT_FACE",FACE,{"disambiguationData":[OSD([sQuery(id+"F21.wireOp",EDGE,"E55")])]}),"instanceName":"1"});
            extrude(context, id + "F34", {"entities" : qUnion([Q0]), "endBound" : BoundingType.UP_TO_SURFACE, "endBoundEntityFace" : qUnion([Q1]), "depth" : 25.4 * mm});
        }
        {
            var Q0;
            Q0=makeQuery(id+"F18.opExtrude","CAP_FACE",FACE,{"disambiguationData":[OSD([sQuery(id+"F17.wireOp",EDGE,"E18.bottom"),sQuery(id+"F17.wireOp",EDGE,"E18.top"),sQuery(id+"F17.wireOp",EDGE,"E18.left"),sQuery(id+"F17.wireOp",EDGE,"E18.right")])],"isStart":true});
            var sketch = newSketch(context, id + "F35", { "sketchPlane" : qUnion([Q0])});
            skPoint(sketch, "E150", {"position": v(-2231.13, -474.17) * mm});
            skPoint(sketch, "E151", {"position": v(-2231.13, 872.03) * mm});
            skPoint(sketch, "E152.0", {"position": v(766.07, 872.03) * mm});
            skPoint(sketch, "E153.0", {"position": v(766.07, -474.17) * mm});
            skLineSegment(sketch, "E154.bottom", {"start": v(-2231.13, 872.03) * mm, "end": v(-2091.43, 872.03) * mm});
            skLineSegment(sketch, "E154.top", {"start": v(-2231.13, 833.93) * mm, "end": v(-2091.43, 833.93) * mm});
            skLineSegment(sketch, "E154.left", {"start": v(-2231.13, 872.03) * mm, "end": v(-2231.13, 833.93) * mm});
            skLineSegment(sketch, "E154.right", {"start": v(-2091.43, 872.03) * mm, "end": v(-2091.43, 833.93) * mm});
            skLineSegment(sketch, "E155.bottom", {"start": v(766.07, 872.03) * mm, "end": v(626.37, 872.03) * mm});
            skLineSegment(sketch, "E155.top", {"start": v(766.07, 833.93) * mm, "end": v(626.37, 833.93) * mm});
            skLineSegment(sketch, "E155.left", {"start": v(766.07, 872.03) * mm, "end": v(766.07, 833.93) * mm});
            skLineSegment(sketch, "E155.right", {"start": v(626.37, 872.03) * mm, "end": v(626.37, 833.93) * mm});
            skLineSegment(sketch, "E156.bottom", {"start": v(766.07, -474.17) * mm, "end": v(626.37, -474.17) * mm});
            skLineSegment(sketch, "E156.top", {"start": v(766.07, -436.07) * mm, "end": v(626.37, -436.07) * mm});
            skLineSegment(sketch, "E156.left", {"start": v(766.07, -474.17) * mm, "end": v(766.07, -436.07) * mm});
            skLineSegment(sketch, "E156.right", {"start": v(626.37, -474.17) * mm, "end": v(626.37, -436.07) * mm});
            skLineSegment(sketch, "E157.bottom", {"start": v(-2231.13, -474.17) * mm, "end": v(-2091.43, -474.17) * mm});
            skLineSegment(sketch, "E157.top", {"start": v(-2231.13, -436.07) * mm, "end": v(-2091.43, -436.07) * mm});
            skLineSegment(sketch, "E157.left", {"start": v(-2231.13, -474.17) * mm, "end": v(-2231.13, -436.07) * mm});
            skLineSegment(sketch, "E157.right", {"start": v(-2091.43, -474.17) * mm, "end": v(-2091.43, -436.07) * mm});
            skSolve(sketch);
        }
        {
            var Q0;
            Q0 = qSketchRegion(id + "F35", true);
            var Q1;
            {Q1=qUnion([makeQuery(id+"F34.opExtrude","CAP_FACE",FACE,{"disambiguationData":[OSD([sQuery(id+"F33.wireOp",EDGE,"E143.bottom"),sQuery(id+"F33.wireOp",EDGE,"E143.top"),sQuery(id+"F33.wireOp",EDGE,"E143.left"),sQuery(id+"F33.wireOp",EDGE,"E143.right")])],"isStart":false}),makeQuery(id+"F34.opExtrude","CAP_FACE",FACE,{"disambiguationData":[OSD([sQuery(id+"F33.wireOp",EDGE,"E145.bottom"),sQuery(id+"F33.wireOp",EDGE,"E145.top"),sQuery(id+"F33.wireOp",EDGE,"E145.left"),sQuery(id+"F33.wireOp",EDGE,"E145.right")])],"isStart":false}),makeQuery(id+"F34.opExtrude","CAP_FACE",FACE,{"disambiguationData":[OSD([sQuery(id+"F33.wireOp",EDGE,"E147.bottom"),sQuery(id+"F33.wireOp",EDGE,"E147.top"),sQuery(id+"F33.wireOp",EDGE,"E147.left"),sQuery(id+"F33.wireOp",EDGE,"E147.right")])],"isStart":false}),makeQuery(id+"F34.opExtrude","CAP_FACE",FACE,{"disambiguationData":[OSD([sQuery(id+"F33.wireOp",EDGE,"E149.bottom"),sQuery(id+"F33.wireOp",EDGE,"E149.top"),sQuery(id+"F33.wireOp",EDGE,"E149.left"),sQuery(id+"F33.wireOp",EDGE,"E149.right")])],"isStart":false})]);}
            extrude(context, id + "F36", {"entities" : qUnion([Q0]), "endBound" : BoundingType.UP_TO_SURFACE, "oppositeDirection" : true, "endBoundEntityFace" : qUnion([Q1]), "depth" : 25.4 * mm});
        }
        {
            var Q0;
            Q0=makeQuery(id+"F18.opExtrude","SWEPT_BODY",BODY,{"disambiguationData":[OSD([sQuery(id+"F17.wireOp",EDGE,"E18.bottom"),sQuery(id+"F17.wireOp",EDGE,"E18.top"),sQuery(id+"F17.wireOp",EDGE,"E18.left"),sQuery(id+"F17.wireOp",EDGE,"E18.right")])]});
            var Q1;
            Q1=makeQuery(id+"F18.opExtrude","SWEPT_BODY",BODY,{"disambiguationData":[OSD([sQuery(id+"F17.wireOp",EDGE,"E19.bottom"),sQuery(id+"F17.wireOp",EDGE,"E19.top"),sQuery(id+"F17.wireOp",EDGE,"E19.left"),sQuery(id+"F17.wireOp",EDGE,"E19.right")])]});
            var Q2;
            Q2=makeQuery(id+"F36.opExtrude","SWEPT_BODY",BODY,{"disambiguationData":[OSD([sQuery(id+"F35.wireOp",EDGE,"E157.bottom"),sQuery(id+"F35.wireOp",EDGE,"E157.top"),sQuery(id+"F35.wireOp",EDGE,"E157.left"),sQuery(id+"F35.wireOp",EDGE,"E157.right")])]});
            var Q3;
            Q3=makeQuery(id+"F36.opExtrude","SWEPT_BODY",BODY,{"disambiguationData":[OSD([sQuery(id+"F35.wireOp",EDGE,"E154.bottom"),sQuery(id+"F35.wireOp",EDGE,"E154.top"),sQuery(id+"F35.wireOp",EDGE,"E154.left"),sQuery(id+"F35.wireOp",EDGE,"E154.right")])]});
            var Q4;
            Q4=makeQuery(id+"F36.opExtrude","SWEPT_BODY",BODY,{"disambiguationData":[OSD([sQuery(id+"F35.wireOp",EDGE,"E155.bottom"),sQuery(id+"F35.wireOp",EDGE,"E155.top"),sQuery(id+"F35.wireOp",EDGE,"E155.left"),sQuery(id+"F35.wireOp",EDGE,"E155.right")])]});
            var Q5;
            Q5=makeQuery(id+"F36.opExtrude","SWEPT_BODY",BODY,{"disambiguationData":[OSD([sQuery(id+"F35.wireOp",EDGE,"E156.bottom"),sQuery(id+"F35.wireOp",EDGE,"E156.top"),sQuery(id+"F35.wireOp",EDGE,"E156.left"),sQuery(id+"F35.wireOp",EDGE,"E156.right")])]});
            booleanBodies(context, id + "F37", {"operationType" : BooleanOperationType.SUBTRACTION, "tools" : qUnion([Q0, Q1]), "targets" : qUnion([Q2, Q3, Q4, Q5]), "keepTools" : true});
        }
        {
            var Q0;
            Q0=makeQuery(id+"F9.opExtrude","CAP_FACE",FACE,{"disambiguationData":[OSD([sQuery(id+"F8.wireOp",EDGE,"E12.bottom"),sQuery(id+"F8.wireOp",EDGE,"E12.top"),sQuery(id+"F8.wireOp",EDGE,"E12.left"),sQuery(id+"F8.wireOp",EDGE,"E12.right")])],"isStart":true});
            var sketch = newSketch(context, id + "F38", { "sketchPlane" : qUnion([Q0])});
            skCircle(sketch, "E158", {"center": v(368.7, 1294.18) * mm, "radius": 269.75 * mm});
            skSolve(sketch);
        }
        {
            var Q0;
            Q0 = qSketchRegion(id + "F38", true);
            extrude(context, id + "F39", {"entities" : qUnion([Q0]), "depth" : 1828.8 * mm});
        }
        {
            var Q0;
            Q0=makeQuery(id+"F9.opExtrude","CAP_FACE",FACE,{"disambiguationData":[OSD([sQuery(id+"F8.wireOp",EDGE,"E12.bottom"),sQuery(id+"F8.wireOp",EDGE,"E12.top"),sQuery(id+"F8.wireOp",EDGE,"E12.left"),sQuery(id+"F8.wireOp",EDGE,"E12.right")])],"isStart":true});
            var sketch = newSketch(context, id + "F40", { "sketchPlane" : qUnion([Q0])});
            skCircle(sketch, "E159", {"center": v(-158.64, 1344.65) * mm, "radius": 198.57 * mm});
            skSolve(sketch);
        }
        {
            var Q0;
            Q0 = qSketchRegion(id + "F40", true);
            extrude(context, id + "F41", {"entities" : qUnion([Q0]), "depth" : 1600.2 * mm});
        }
        {
            var Q0;
            Q0=makeQuery(id+"F32.opExtrude","SWEPT_EDGE",EDGE,{"disambiguationData":[OSD([sQuery(id+"F31.wireOp",EDGE,"E104"),sQuery(id+"F31.wireOp",EDGE,"E105")])]});
            var Q1;
            Q1=makeQuery(id+"F32.opExtrude","SWEPT_EDGE",EDGE,{"disambiguationData":[OSD([sQuery(id+"F31.wireOp",EDGE,"E105"),sQuery(id+"F31.wireOp",EDGE,"E106")])]});
            var Q2;
            Q2=makeQuery(id+"F32.opExtrude","SWEPT_EDGE",EDGE,{"disambiguationData":[OSD([sQuery(id+"F31.wireOp",EDGE,"E110"),sQuery(id+"F31.wireOp",EDGE,"E111")])]});
            var Q3;
            Q3=makeQuery(id+"F32.opExtrude","SWEPT_EDGE",EDGE,{"disambiguationData":[OSD([sQuery(id+"F31.wireOp",EDGE,"E111"),sQuery(id+"F31.wireOp",EDGE,"E112")])]});
            var Q4;
            Q4=makeQuery(id+"F32.opExtrude","SWEPT_EDGE",EDGE,{"disambiguationData":[OSD([sQuery(id+"F31.wireOp",EDGE,"E107"),sQuery(id+"F31.wireOp",EDGE,"E108")])]});
            var Q5;
            Q5=makeQuery(id+"F32.opExtrude","SWEPT_EDGE",EDGE,{"disambiguationData":[OSD([sQuery(id+"F31.wireOp",EDGE,"E137.top"),sQuery(id+"F31.wireOp",EDGE,"E137.right")])]});
            var Q6;
            Q6=makeQuery(id+"F32.opExtrude","SWEPT_EDGE",EDGE,{"disambiguationData":[OSD([sQuery(id+"F31.wireOp",EDGE,"E108"),sQuery(id+"F31.wireOp",EDGE,"E109")])]});
            var Q7;
            Q7=makeQuery(id+"F32.opExtrude","SWEPT_EDGE",EDGE,{"disambiguationData":[OSD([sQuery(id+"F31.wireOp",EDGE,"E109"),sQuery(id+"F31.wireOp",EDGE,"E110")])]});
            var Q8;
            Q8=makeQuery(id+"F32.opExtrude","SWEPT_EDGE",EDGE,{"disambiguationData":[OSD([sQuery(id+"F31.wireOp",EDGE,"E106"),sQuery(id+"F31.wireOp",EDGE,"E107")])]});
            var Q9;
            Q9=makeQuery(id+"F32.opExtrude","SWEPT_EDGE",EDGE,{"disambiguationData":[OSD([sQuery(id+"F31.wireOp",EDGE,"E137.top"),sQuery(id+"F31.wireOp",EDGE,"E137.left")])]});
            var Q10;
            Q10=makeQuery(id+"F32.opExtrude","SWEPT_EDGE",EDGE,{"disambiguationData":[OSD([sQuery(id+"F31.wireOp",EDGE,"E137.bottom"),sQuery(id+"F31.wireOp",EDGE,"E137.right")])]});
            var Q11;
            Q11=makeQuery(id+"F32.opExtrude","SWEPT_EDGE",EDGE,{"disambiguationData":[OSD([sQuery(id+"F31.wireOp",EDGE,"E137.bottom"),sQuery(id+"F31.wireOp",EDGE,"E137.left")])]});
            var Q12;
            Q12=makeQuery(id+"F32.opExtrude","SWEPT_EDGE",EDGE,{"disambiguationData":[OSD([sQuery(id+"F31.wireOp",EDGE,"E112"),sQuery(id+"F31.wireOp",EDGE,"E113")])]});
            var Q13;
            Q13=makeQuery(id+"F32.opExtrude","SWEPT_EDGE",EDGE,{"disambiguationData":[OSD([sQuery(id+"F31.wireOp",EDGE,"E139.top"),sQuery(id+"F31.wireOp",EDGE,"E139.left")])]});
            var Q14;
            Q14=makeQuery(id+"F32.opExtrude","SWEPT_EDGE",EDGE,{"disambiguationData":[OSD([sQuery(id+"F31.wireOp",EDGE,"E140.top"),sQuery(id+"F31.wireOp",EDGE,"E140.left")])]});
            var Q15;
            Q15=makeQuery(id+"F32.opExtrude","SWEPT_EDGE",EDGE,{"disambiguationData":[OSD([sQuery(id+"F31.wireOp",EDGE,"E114"),sQuery(id+"F31.wireOp",EDGE,"E115")])]});
            var Q16;
            Q16=makeQuery(id+"F32.opExtrude","SWEPT_EDGE",EDGE,{"disambiguationData":[OSD([sQuery(id+"F31.wireOp",EDGE,"E115"),sQuery(id+"F31.wireOp",EDGE,"E116")])]});
            var Q17;
            Q17=makeQuery(id+"F32.opExtrude","SWEPT_EDGE",EDGE,{"disambiguationData":[OSD([sQuery(id+"F31.wireOp",EDGE,"E116"),sQuery(id+"F31.wireOp",EDGE,"E117")])]});
            var Q18;
            Q18=makeQuery(id+"F32.opExtrude","SWEPT_EDGE",EDGE,{"disambiguationData":[OSD([sQuery(id+"F31.wireOp",EDGE,"E118"),sQuery(id+"F31.wireOp",EDGE,"E119")])]});
            var Q19;
            Q19=makeQuery(id+"F32.opExtrude","SWEPT_EDGE",EDGE,{"disambiguationData":[OSD([sQuery(id+"F31.wireOp",EDGE,"E119"),sQuery(id+"F31.wireOp",EDGE,"E120")])]});
            var Q20;
            Q20=makeQuery(id+"F32.opExtrude","SWEPT_EDGE",EDGE,{"disambiguationData":[OSD([sQuery(id+"F31.wireOp",EDGE,"E120"),sQuery(id+"F31.wireOp",EDGE,"E121")])]});
            var Q21;
            Q21=makeQuery(id+"F32.opExtrude","SWEPT_EDGE",EDGE,{"disambiguationData":[OSD([sQuery(id+"F31.wireOp",EDGE,"E122"),sQuery(id+"F31.wireOp",EDGE,"E123")])]});
            var Q22;
            Q22=makeQuery(id+"F32.opExtrude","SWEPT_EDGE",EDGE,{"disambiguationData":[OSD([sQuery(id+"F31.wireOp",EDGE,"E123"),sQuery(id+"F31.wireOp",EDGE,"E124")])]});
            var Q23;
            Q23=makeQuery(id+"F32.opExtrude","SWEPT_EDGE",EDGE,{"disambiguationData":[OSD([sQuery(id+"F31.wireOp",EDGE,"E124"),sQuery(id+"F31.wireOp",EDGE,"E125")])]});
            var Q24;
            Q24=makeQuery(id+"F32.opExtrude","SWEPT_EDGE",EDGE,{"disambiguationData":[OSD([sQuery(id+"F31.wireOp",EDGE,"E126"),sQuery(id+"F31.wireOp",EDGE,"E127")])]});
            var Q25;
            Q25=makeQuery(id+"F32.opExtrude","SWEPT_EDGE",EDGE,{"disambiguationData":[OSD([sQuery(id+"F31.wireOp",EDGE,"E129"),sQuery(id+"F31.wireOp",EDGE,"E130")])]});
            var Q26;
            Q26=makeQuery(id+"F32.opExtrude","SWEPT_EDGE",EDGE,{"disambiguationData":[OSD([sQuery(id+"F31.wireOp",EDGE,"E132"),sQuery(id+"F31.wireOp",EDGE,"E133")])]});
            var Q27;
            Q27=makeQuery(id+"F32.opExtrude","SWEPT_EDGE",EDGE,{"disambiguationData":[OSD([sQuery(id+"F31.wireOp",EDGE,"E133"),sQuery(id+"F31.wireOp",EDGE,"E134")])]});
            var Q28;
            Q28=makeQuery(id+"F32.opExtrude","SWEPT_EDGE",EDGE,{"disambiguationData":[OSD([sQuery(id+"F31.wireOp",EDGE,"E131"),sQuery(id+"F31.wireOp",EDGE,"E132")])]});
            var Q29;
            Q29=makeQuery(id+"F32.opExtrude","SWEPT_EDGE",EDGE,{"disambiguationData":[OSD([sQuery(id+"F31.wireOp",EDGE,"E135"),sQuery(id+"F31.wireOp",EDGE,"E136")])]});
            var Q30;
            Q30=makeQuery(id+"F32.opExtrude","SWEPT_EDGE",EDGE,{"disambiguationData":[OSD([sQuery(id+"F31.wireOp",EDGE,"E134"),sQuery(id+"F31.wireOp",EDGE,"E135")])]});
            var Q31;
            Q31=makeQuery(id+"F32.opExtrude","SWEPT_EDGE",EDGE,{"disambiguationData":[OSD([sQuery(id+"F31.wireOp",EDGE,"E138.top"),sQuery(id+"F31.wireOp",EDGE,"E138.left")])]});
            var Q32;
            Q32=makeQuery(id+"F32.opExtrude","SWEPT_EDGE",EDGE,{"disambiguationData":[OSD([sQuery(id+"F31.wireOp",EDGE,"E138.bottom"),sQuery(id+"F31.wireOp",EDGE,"E138.left")])]});
            var Q33;
            Q33=makeQuery(id+"F32.opExtrude","SWEPT_EDGE",EDGE,{"disambiguationData":[OSD([sQuery(id+"F31.wireOp",EDGE,"E138.top"),sQuery(id+"F31.wireOp",EDGE,"E138.right")])]});
            var Q34;
            Q34=makeQuery(id+"F32.opExtrude","SWEPT_EDGE",EDGE,{"disambiguationData":[OSD([sQuery(id+"F31.wireOp",EDGE,"E138.bottom"),sQuery(id+"F31.wireOp",EDGE,"E138.right")])]});
            var Q35;
            Q35=makeQuery(id+"F32.opExtrude","SWEPT_EDGE",EDGE,{"disambiguationData":[OSD([sQuery(id+"F31.wireOp",EDGE,"E121"),sQuery(id+"F31.wireOp",EDGE,"E122")])]});
            var Q36;
            Q36=makeQuery(id+"F32.opExtrude","SWEPT_EDGE",EDGE,{"disambiguationData":[OSD([sQuery(id+"F31.wireOp",EDGE,"E125"),sQuery(id+"F31.wireOp",EDGE,"E126")])]});
            var Q37;
            Q37=makeQuery(id+"F32.opExtrude","SWEPT_EDGE",EDGE,{"disambiguationData":[OSD([sQuery(id+"F31.wireOp",EDGE,"E117"),sQuery(id+"F31.wireOp",EDGE,"E118")])]});
            var Q38;
            Q38=makeQuery(id+"F32.opExtrude","SWEPT_EDGE",EDGE,{"disambiguationData":[OSD([sQuery(id+"F31.wireOp",EDGE,"E113"),sQuery(id+"F31.wireOp",EDGE,"E114")])]});
            var Q39;
            Q39=makeQuery(id+"F32.opExtrude","SWEPT_EDGE",EDGE,{"disambiguationData":[OSD([sQuery(id+"F31.wireOp",EDGE,"E136"),sQuery(id+"F31.wireOp",EDGE,"E141")])]});
            var Q40;
            Q40=makeQuery(id+"F32.opExtrude","SWEPT_EDGE",EDGE,{"disambiguationData":[OSD([sQuery(id+"F31.wireOp",EDGE,"E140.top"),sQuery(id+"F31.wireOp",EDGE,"E140.right")])]});
            var Q41;
            Q41=makeQuery(id+"F32.opExtrude","SWEPT_EDGE",EDGE,{"disambiguationData":[OSD([sQuery(id+"F31.wireOp",EDGE,"E140.bottom"),sQuery(id+"F31.wireOp",EDGE,"E140.right")])]});
            var Q42;
            Q42=makeQuery(id+"F32.opExtrude","SWEPT_EDGE",EDGE,{"disambiguationData":[OSD([sQuery(id+"F31.wireOp",EDGE,"E140.bottom"),sQuery(id+"F31.wireOp",EDGE,"E140.left")])]});
            var Q43;
            Q43=makeQuery(id+"F32.opExtrude","SWEPT_EDGE",EDGE,{"disambiguationData":[OSD([sQuery(id+"F31.wireOp",EDGE,"E139.bottom"),sQuery(id+"F31.wireOp",EDGE,"E139.left")])]});
            var Q44;
            Q44=makeQuery(id+"F32.opExtrude","SWEPT_EDGE",EDGE,{"disambiguationData":[OSD([sQuery(id+"F31.wireOp",EDGE,"E139.bottom"),sQuery(id+"F31.wireOp",EDGE,"E139.right")])]});
            var Q45;
            Q45=makeQuery(id+"F32.opExtrude","SWEPT_EDGE",EDGE,{"disambiguationData":[OSD([sQuery(id+"F31.wireOp",EDGE,"E139.top"),sQuery(id+"F31.wireOp",EDGE,"E139.right")])]});
            fillet(context, id + "F42", {"entities" : qUnion([Q0, Q1, Q2, Q3, Q4, Q5, Q6, Q7, Q8, Q9, Q10, Q11, Q12, Q13, Q14, Q15, Q16, Q17, Q18, Q19, Q20, Q21, Q22, Q23, Q24, Q25, Q26, Q27, Q28, Q29, Q30, Q31, Q32, Q33, Q34, Q35, Q36, Q37, Q38, Q39, Q40, Q41, Q42, Q43, Q44, Q45]), "radius" : 3.17 * mm, "tangentPropagation" : true, "allowEdgeOverflow" : false});
        }
        {
            var Q0;
            Q0=makeQuery(id+"F18.opExtrude","SWEPT_FACE",FACE,{"disambiguationData":[OSD([sQuery(id+"F17.wireOp",EDGE,"E19.left")])]});
            var sketch = newSketch(context, id + "F43", { "sketchPlane" : qUnion([Q0])});
            skLineSegment(sketch, "E160.0", {"start": v(-436.07, 0) * mm, "end": v(-436.07, 1377.95) * mm, "construction": true});
            skLineSegment(sketch, "E161.0", {"start": v(-474.17, 1377.95) * mm, "end": v(872.03, 1377.95) * mm, "construction": true});
            skLineSegment(sketch, "E162", {"start": v(-436.07, 839.13) * mm, "end": v(102.74, 1377.95) * mm});
            skLineSegment(sketch, "E163", {"start": v(102.74, 1377.95) * mm, "end": v(-22.98, 1377.95) * mm});
            skLineSegment(sketch, "E164", {"start": v(-22.98, 1377.95) * mm, "end": v(-436.07, 964.86) * mm});
            skLineSegment(sketch, "E165", {"start": v(-436.07, 964.86) * mm, "end": v(-436.07, 839.13) * mm});
            skLineSegment(sketch, "E166", {"start": v(198.93, 1377.95) * mm, "end": v(198.93, 190.99) * mm, "construction": true});
            skLineSegment(sketch, "E167.MirrorCS", {"start": v(833.93, 839.13) * mm, "end": v(295.11, 1377.95) * mm});
            skLineSegment(sketch, "E168.MirrorCS", {"start": v(420.83, 1377.95) * mm, "end": v(833.93, 964.86) * mm});
            skLineSegment(sketch, "E169", {"start": v(833.93, 964.86) * mm, "end": v(833.93, 839.13) * mm});
            skLineSegment(sketch, "E170", {"start": v(295.11, 1377.95) * mm, "end": v(420.83, 1377.95) * mm});
            skSolve(sketch);
        }
        {
            var Q0;
            Q0 = qSketchRegion(id + "F43", true);
            extrude(context, id + "F44", {"entities" : qUnion([Q0]), "oppositeDirection" : true, "depth" : 38.1 * mm});
        }
        {
            var Q0;
            Q0=makeQuery(id+"F18.opExtrude","SWEPT_FACE",FACE,{"disambiguationData":[OSD([sQuery(id+"F17.wireOp",EDGE,"E18.left")])]});
            var sketch = newSketch(context, id + "F45", { "sketchPlane" : qUnion([Q0])});
            skLineSegment(sketch, "E171.0", {"start": v(-420.83, 1377.95) * mm, "end": v(-833.93, 964.86) * mm});
            skLineSegment(sketch, "E172.0.1", {"start": v(-833.93, 964.86) * mm, "end": v(-833.93, 839.13) * mm});
            skLineSegment(sketch, "E172.0.2", {"start": v(-833.93, 839.13) * mm, "end": v(-295.11, 1377.95) * mm});
            skLineSegment(sketch, "E172.0.3", {"start": v(-295.11, 1377.95) * mm, "end": v(-420.83, 1377.95) * mm});
            skLineSegment(sketch, "E173.0.0", {"start": v(22.98, 1377.95) * mm, "end": v(-102.74, 1377.95) * mm});
            skLineSegment(sketch, "E173.0.1", {"start": v(-102.74, 1377.95) * mm, "end": v(436.07, 839.13) * mm});
            skLineSegment(sketch, "E173.0.2", {"start": v(436.07, 839.13) * mm, "end": v(436.07, 964.86) * mm});
            skLineSegment(sketch, "E173.0.3", {"start": v(436.07, 964.86) * mm, "end": v(22.98, 1377.95) * mm});
            skSolve(sketch);
        }
        {
            var Q0;
            Q0 = qSketchRegion(id + "F45", true);
            extrude(context, id + "F46", {"entities" : qUnion([Q0]), "oppositeDirection" : true, "depth" : 38.1 * mm});
        }
    });
